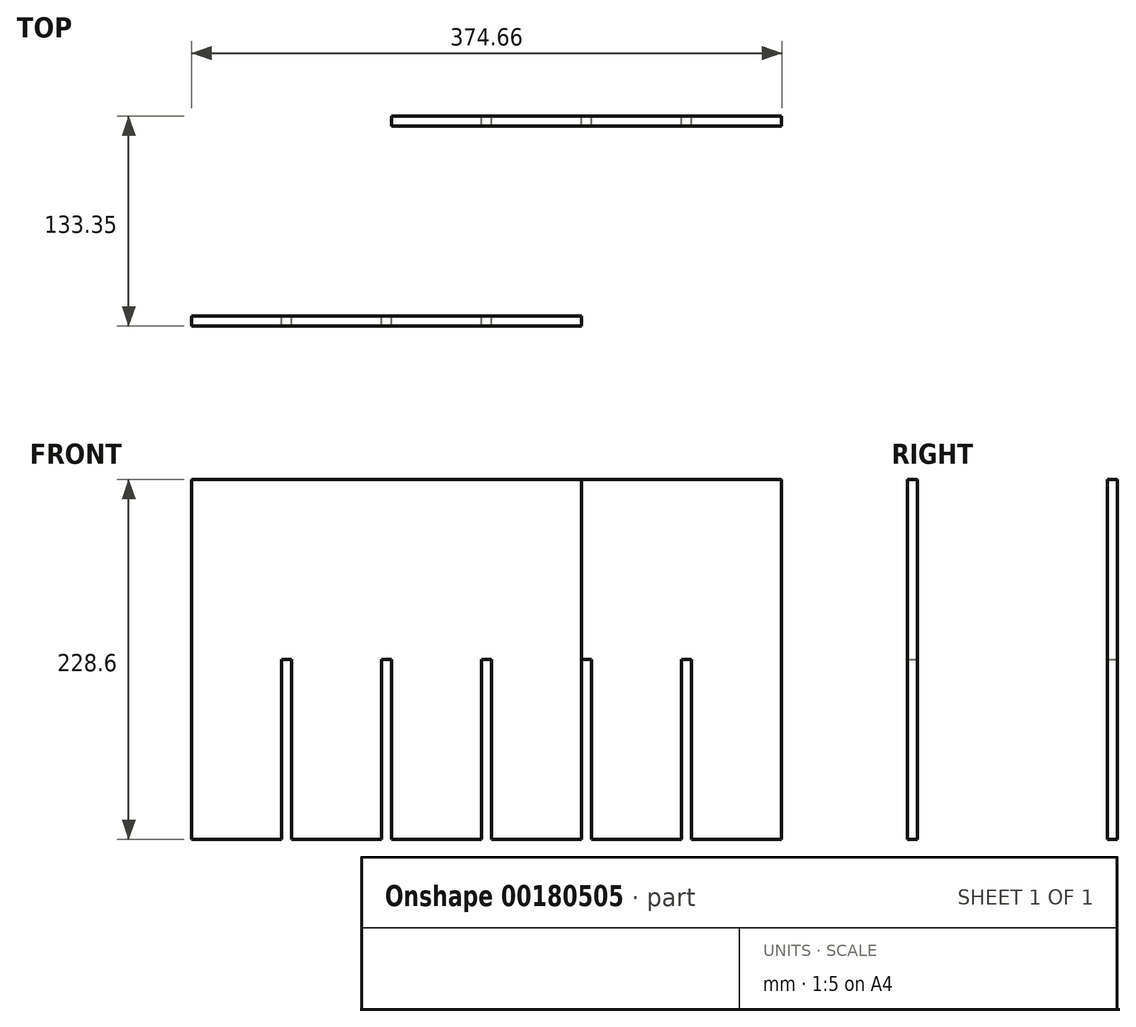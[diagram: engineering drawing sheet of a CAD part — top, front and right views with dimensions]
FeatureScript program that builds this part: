
annotation { "Feature Type Name" : "Feature", "Feature Type Description" : "" }
export const myFeature = defineFeature(function(context is Context, id is Id, definition is map)
    precondition{}
    {
        {
            var Q0;
            Q0=qCreatedBy(makeId("Front.planeOp"),FACE);
            var sketch = newSketch(context, id + "F0", { "sketchPlane" : qUnion([Q0])});
            skLineSegment(sketch, "E0.bottom", {"start": v(123.82, -114.3) * mm, "end": v(66.67, -114.3) * mm});
            skLineSegment(sketch, "E0.top", {"start": v(123.83, 114.3) * mm, "end": v(-123.83, 114.3) * mm});
            skLineSegment(sketch, "E0.left", {"start": v(123.83, -114.3) * mm, "end": v(123.83, 114.3) * mm});
            skLineSegment(sketch, "E0.right", {"start": v(-123.83, -114.3) * mm, "end": v(-123.83, 114.3) * mm});
            skPoint(sketch, "E0.middle", {"position": v(0, 0) * mm});
            skLineSegment(sketch, "E1", {"start": v(0, 114.3) * mm, "end": v(0, -114.3) * mm, "construction": true});
            skLineSegment(sketch, "E2.0", {"start": v(-3.18, 0) * mm, "end": v(-3.18, -114.3) * mm});
            skLineSegment(sketch, "E3.0", {"start": v(-66.68, 0) * mm, "end": v(-66.67, -114.3) * mm});
            skLineSegment(sketch, "E4.0", {"start": v(-60.33, 0) * mm, "end": v(-60.33, -114.3) * mm});
            skLineSegment(sketch, "E5.MirrorCS", {"start": v(3.17, 0) * mm, "end": v(3.17, -114.3) * mm});
            skLineSegment(sketch, "E6.MirrorCS", {"start": v(60.32, 0) * mm, "end": v(60.32, -114.3) * mm});
            skLineSegment(sketch, "E7.MirrorCS", {"start": v(66.67, 0) * mm, "end": v(66.67, -114.3) * mm});
            skLineSegment(sketch, "E8", {"start": v(-66.68, 0) * mm, "end": v(-60.33, 0) * mm});
            skPoint(sketch, "E9.orphan", {"position": v(-66.68, 114.3) * mm});
            skPoint(sketch, "E10.orphan", {"position": v(-60.33, 114.3) * mm});
            skPoint(sketch, "E11.orphan", {"position": v(-3.18, 114.3) * mm});
            skPoint(sketch, "E12.orphan", {"position": v(3.18, 114.3) * mm});
            skPoint(sketch, "E13.orphan", {"position": v(60.33, 114.3) * mm});
            skPoint(sketch, "E14.orphan", {"position": v(66.67, 114.3) * mm});
            skLineSegment(sketch, "E15.trimOffspring", {"start": v(60.33, 0) * mm, "end": v(66.67, 0) * mm});
            skLineSegment(sketch, "E16.trimOffspring", {"start": v(-3.18, 0) * mm, "end": v(3.17, 0) * mm});
            skLineSegment(sketch, "E17.trimOffspring", {"start": v(-66.68, -114.3) * mm, "end": v(-123.83, -114.3) * mm});
            skLineSegment(sketch, "E18.trimOffspring", {"start": v(-3.18, -114.3) * mm, "end": v(-60.32, -114.3) * mm});
            skLineSegment(sketch, "E19.trimOffspring", {"start": v(60.32, -114.3) * mm, "end": v(3.17, -114.3) * mm});
            skSolve(sketch);
        }
        {
            var Q0;
            Q0=qSketchRegion(id+"F0",true);
            extrude(context, id + "F1", {"entities" : qUnion([Q0]), "depth" : 6.35 * mm});
        }
        {
            var Q0;
            Q0=makeQuery(id+"F1.opExtrude","SWEPT_BODY",BODY,{"disambiguationData":[OSD([sQuery(id+"F0.wireOp",EDGE,"E0.bottom"),sQuery(id+"F0.wireOp",EDGE,"E0.top"),sQuery(id+"F0.wireOp",EDGE,"E0.left"),sQuery(id+"F0.wireOp",EDGE,"E0.right"),sQuery(id+"F0.wireOp",EDGE,"E2.0"),sQuery(id+"F0.wireOp",EDGE,"E3.0"),sQuery(id+"F0.wireOp",EDGE,"E4.0"),sQuery(id+"F0.wireOp",EDGE,"E5.MirrorCS"),sQuery(id+"F0.wireOp",EDGE,"E6.MirrorCS"),sQuery(id+"F0.wireOp",EDGE,"E7.MirrorCS"),sQuery(id+"F0.wireOp",EDGE,"E8"),sQuery(id+"F0.wireOp",EDGE,"E15.trimOffspring"),sQuery(id+"F0.wireOp",EDGE,"E16.trimOffspring"),sQuery(id+"F0.wireOp",EDGE,"E17.trimOffspring"),sQuery(id+"F0.wireOp",EDGE,"E18.trimOffspring"),sQuery(id+"F0.wireOp",EDGE,"E19.trimOffspring")])]});
            transform(context, id + "F2", {"entities" : qUnion([Q0]), "transformType" : TransformType.TRANSLATION_3D, "dx" : 127 * mm, "dy" : 127 * mm, "dz" : 0 * mm, "makeCopy" : true});
        }
    });
